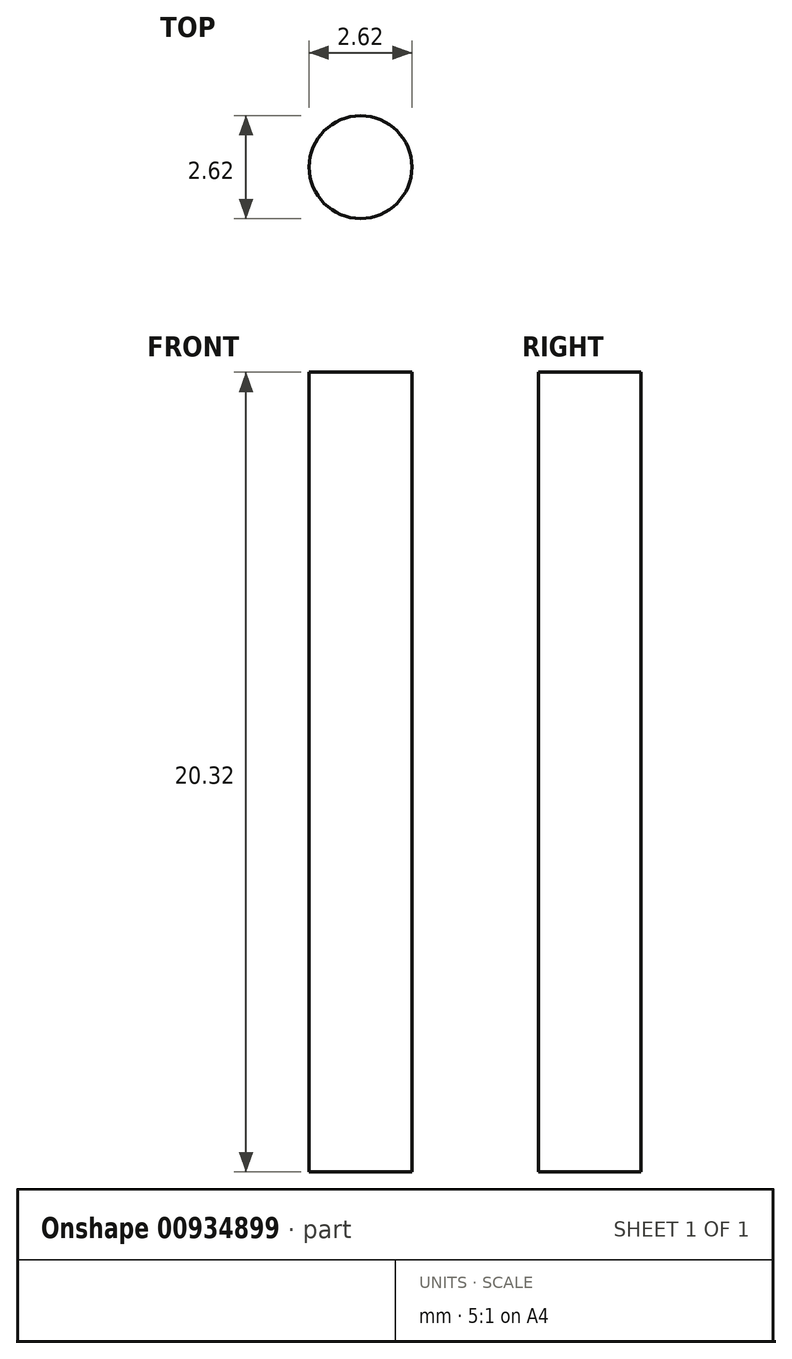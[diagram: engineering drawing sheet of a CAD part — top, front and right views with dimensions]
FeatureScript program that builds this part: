
annotation { "Feature Type Name" : "Feature", "Feature Type Description" : "" }
export const myFeature = defineFeature(function(context is Context, id is Id, definition is map)
    precondition{}
    {
        {
            var Q0;
            Q0=qCreatedBy(makeId("Top.planeOp"),FACE);
            var sketch = newSketch(context, id + "F0", { "sketchPlane" : qUnion([Q0])});
            skCircle(sketch, "E0", {"center": v(0, 0) * mm, "radius": 1.3 * mm});
            skSolve(sketch);
        }
        {
            var Q0;
            Q0 = qSketchRegion(id + "F0", true);
            extrude(context, id + "F1", {"entities" : qUnion([Q0]), "depth" : 20.32 * mm, "offsetDistance" : 25.4 * mm});
        }
    });
